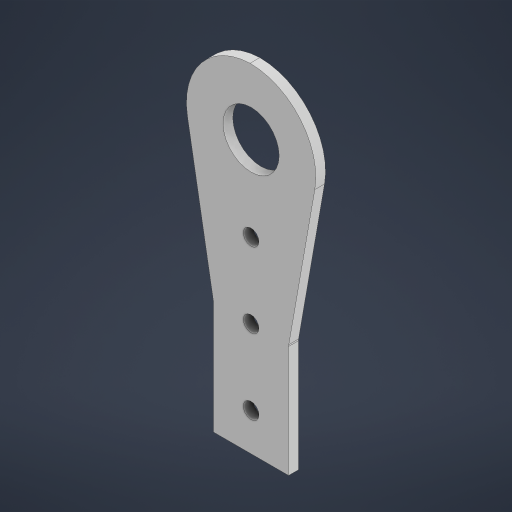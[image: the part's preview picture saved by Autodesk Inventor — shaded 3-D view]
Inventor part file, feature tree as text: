
AUTODESK INVENTOR PART (.ipt)
format: ipt  version: 2024 (Build 280153000, 153)  size: 221,184 bytes
history: native  units: in
note: dims shown in document units (in); Inventor stores cm internally (conversion verified against a paired STEP export)
features: fillet x6, extrude x1, sketch x1
ambient origin geometry x8: Origin, YZ Plane, XZ Plane, XY Plane, X Axis, Y Axis, Z Axis, Center Point
bodies: Solid1 (feature_tree)
feature tree (8):
  extrude  "Extrusion1"  Depth=1.0in
  fillet  "Fillet9"  Radius=0.209in
  fillet  "Fillet10"  Radius=0.209in
  fillet  "Fillet11"  Radius=0.875in
  fillet  "Fillet12"  Radius=2.0in
  fillet  "Fillet13"  Radius=3.0in
  fillet  "Fillet14"  Radius=0.875in
  sketch  "Sketch1"  dims[d0=1.75in d2=0.748in d3=0.209in d4=0.209in d5=0.875in d6=2.0in d7=3.0in d8=0.875in d9=0.875in d10=0.13in d11=0.0in d20=0.5in d21=0.5in d22=0.875in d23=0.875in d24=0.125in d25=0.125in d26=1.0in d27=1.5in d28=1.0in d16=0.0in d17=0.0in d18=0.0in d19=0.0in]
